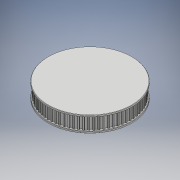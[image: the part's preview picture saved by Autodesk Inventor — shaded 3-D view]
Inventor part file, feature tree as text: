
AUTODESK INVENTOR PART (.ipt)
format: ipt  version: 2018 (Build 220112000, 112)  size: 695,296 bytes
history: native  units: mm
features: extrude x4, sketch x3, other x1, pattern_circular x1, fillet x1
ambient origin geometry x8: Origin, YZ Plane, XZ Plane, XY Plane, X Axis, Y Axis, Z Axis, Center Point
bodies: Solid1 (feature_tree)
feature tree (10):
  other  "Tooth"
  extrude  "Gear Solid Extrusion"  Depth=1.5mm
  extrude  "Tooth Cut-Out Extrusion"  Depth=0.85mm
  pattern_circular  "Teeth Array"  [2 undecoded]
  extrude  "Flange Extrusion Front"  Depth=0.25mm
  extrude  "Flange Extrusion Back"  TaperAngle=0.0deg  [1 undecoded]
  fillet  "Flange Fillet"  Radius=10.0mm
  sketch  "Sketch2"  dims[d2=33.422538mm d3=1.5mm]
  sketch  "Sketch3"  dims[d4=1.14mm d5=0.85mm]
  sketch  "Sketch4"  dims[d6=0.61mm d7=0.25mm d8=2.0mm d11=0.0mm d12=10.0mm d13=0.0mm d14=700.0mm d15=360.0deg d17=34.422538mm d19=0.0mm d20=34.422538mm d21=1.5mm d22=0.0mm d23=0.25mm]
note: 3 required parameter values undecoded (feature->parameter linkage not recoverable at this tier; creation-order binding heuristic only, values carry confidence <= 0.55)
